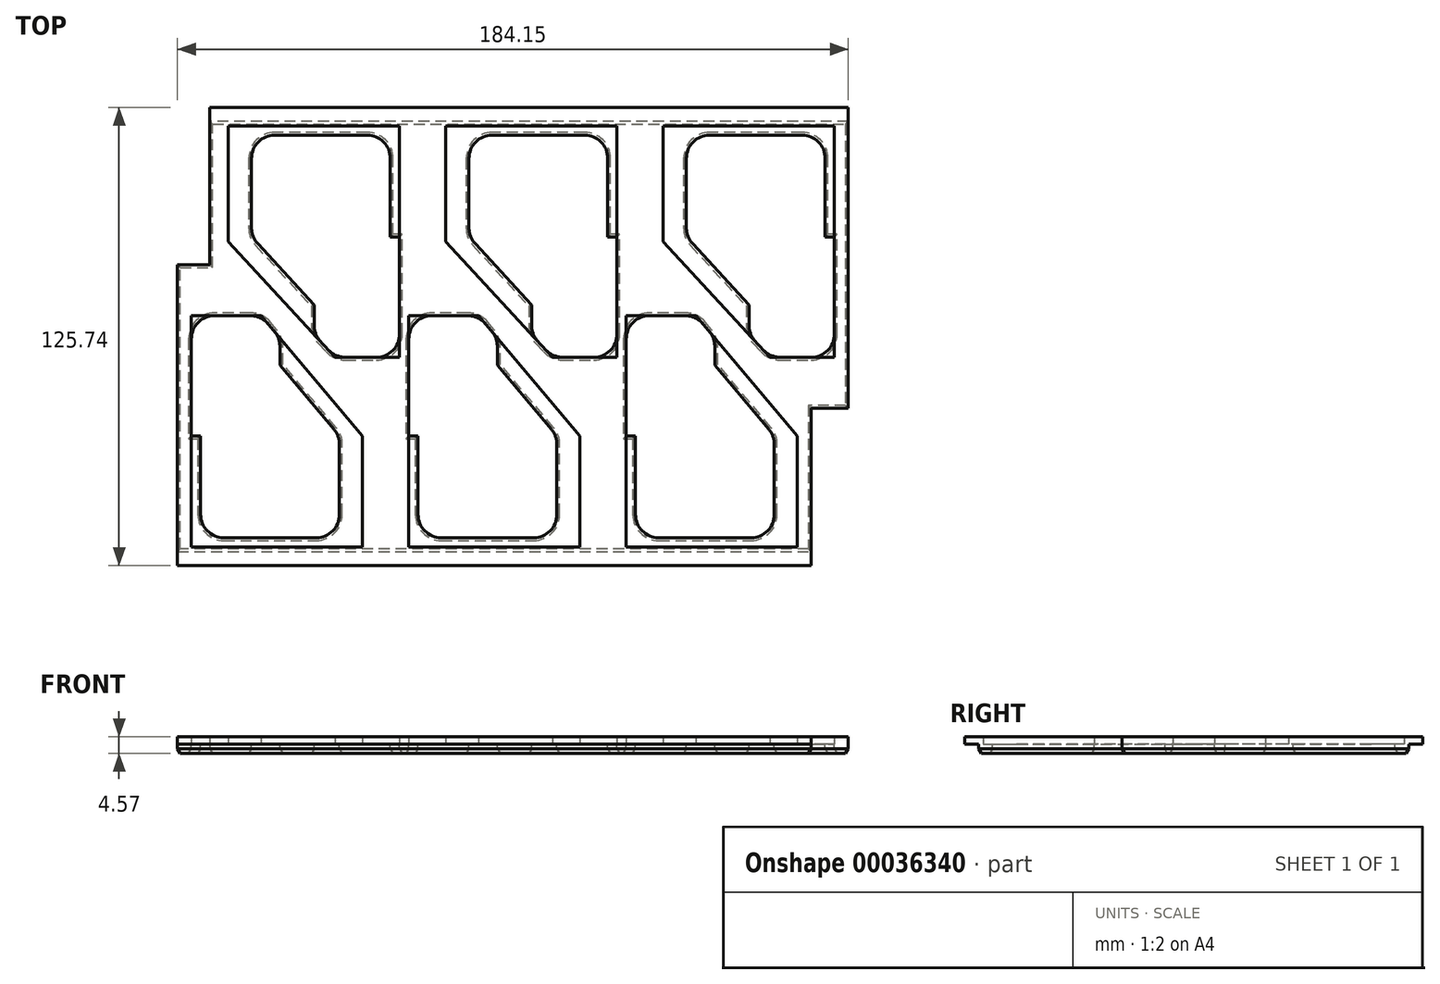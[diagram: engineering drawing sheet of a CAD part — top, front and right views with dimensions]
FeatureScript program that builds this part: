
annotation { "Feature Type Name" : "Feature", "Feature Type Description" : "" }
export const myFeature = defineFeature(function(context is Context, id is Id, definition is map)
    precondition{}
    {
        {
            var Q0;
            Q0=qCreatedBy(makeId("Top.planeOp"),FACE);
            var sketch = newSketch(context, id + "F0", { "sketchPlane" : qUnion([Q0])});
            skLineSegment(sketch, "E0.rect.bottom", {"start": v(-81.28, 62.87) * mm, "end": v(93.98, 62.87) * mm});
            skLineSegment(sketch, "E0.rect.top", {"start": v(-90.17, -62.87) * mm, "end": v(83.82, -62.87) * mm});
            skLineSegment(sketch, "E0.rect.right", {"start": v(93.98, 62.87) * mm, "end": v(93.98, -19.69) * mm});
            skPoint(sketch, "E0.rect.middle", {"position": v(0, 0) * mm});
            skLineSegment(sketch, "E1.MirrorCS", {"start": v(43.18, 57.79) * mm, "end": v(90.17, 57.79) * mm});
            skLineSegment(sketch, "E2.MirrorCS", {"start": v(72.45, -5.71) * mm, "end": v(90.17, -5.71) * mm});
            skLineSegment(sketch, "E3.MirrorCS", {"start": v(-16.51, 26.04) * mm, "end": v(12.76, -5.71) * mm});
            skLineSegment(sketch, "E4.MirrorCS", {"start": v(12.76, -5.71) * mm, "end": v(30.48, -5.71) * mm});
            skLineSegment(sketch, "E5.MirrorCS", {"start": v(-16.51, 57.79) * mm, "end": v(-16.5, 26.04) * mm});
            skLineSegment(sketch, "E6.MirrorCS", {"start": v(30.48, 57.79) * mm, "end": v(30.48, -5.71) * mm});
            skLineSegment(sketch, "E7.MirrorCS", {"start": v(-76.2, 26.04) * mm, "end": v(-46.93, -5.71) * mm});
            skLineSegment(sketch, "E8.MirrorCS", {"start": v(-76.2, 57.79) * mm, "end": v(-76.2, 26.04) * mm});
            skLineSegment(sketch, "E9.MirrorCS", {"start": v(-46.93, -5.71) * mm, "end": v(-29.21, -5.71) * mm});
            skLineSegment(sketch, "E10.MirrorCS", {"start": v(-29.21, 57.79) * mm, "end": v(-29.2, -5.71) * mm});
            skLineSegment(sketch, "E11.MirrorCS", {"start": v(-76.2, 57.79) * mm, "end": v(-29.21, 57.79) * mm});
            skLineSegment(sketch, "E12.MirrorCS", {"start": v(90.17, 57.79) * mm, "end": v(90.17, -5.71) * mm});
            skLineSegment(sketch, "E13.MirrorCS", {"start": v(43.18, 57.79) * mm, "end": v(43.18, 26.04) * mm});
            skLineSegment(sketch, "E14.MirrorCS", {"start": v(43.18, 26.04) * mm, "end": v(72.45, -5.72) * mm});
            skLineSegment(sketch, "E15.MirrorCS", {"start": v(-16.51, 57.79) * mm, "end": v(30.48, 57.79) * mm});
            skLineSegment(sketch, "E16.bottom", {"start": v(-39.37, -57.78) * mm, "end": v(-86.36, -57.79) * mm});
            skLineSegment(sketch, "E16.top", {"start": v(-67.2, 5.71) * mm, "end": v(-86.36, 5.71) * mm});
            skLineSegment(sketch, "E16.left", {"start": v(-39.37, -57.79) * mm, "end": v(-39.37, -27.3) * mm});
            skLineSegment(sketch, "E16.right", {"start": v(-86.36, -57.79) * mm, "end": v(-86.36, 5.72) * mm});
            skLineSegment(sketch, "E17", {"start": v(-67.2, 5.72) * mm, "end": v(-39.37, -27.3) * mm});
            skLineSegment(sketch, "E18.right", {"start": v(-26.67, -57.79) * mm, "end": v(-26.67, 5.72) * mm});
            skLineSegment(sketch, "E18.top", {"start": v(-7.5, 5.72) * mm, "end": v(-26.67, 5.72) * mm});
            skLineSegment(sketch, "E19", {"start": v(-7.5, 5.71) * mm, "end": v(20.32, -27.3) * mm});
            skLineSegment(sketch, "E18.left", {"start": v(20.32, -57.79) * mm, "end": v(20.32, -27.3) * mm});
            skLineSegment(sketch, "E18.bottom", {"start": v(20.32, -57.78) * mm, "end": v(-26.67, -57.78) * mm});
            skLineSegment(sketch, "E20.right", {"start": v(33.02, -57.79) * mm, "end": v(33.02, 5.72) * mm});
            skLineSegment(sketch, "E20.top", {"start": v(52.19, 5.72) * mm, "end": v(33.02, 5.72) * mm});
            skLineSegment(sketch, "E21", {"start": v(52.19, 5.72) * mm, "end": v(80.01, -27.3) * mm});
            skLineSegment(sketch, "E20.left", {"start": v(80.01, -57.79) * mm, "end": v(80.01, -27.3) * mm});
            skLineSegment(sketch, "E20.bottom", {"start": v(80.01, -57.78) * mm, "end": v(33.02, -57.79) * mm});
            skLineSegment(sketch, "E22", {"start": v(93.98, -19.69) * mm, "end": v(83.82, -19.69) * mm});
            skLineSegment(sketch, "E23", {"start": v(83.82, -19.69) * mm, "end": v(83.82, -62.87) * mm});
            skPoint(sketch, "E24.orphan", {"position": v(93.98, -62.87) * mm});
            skLineSegment(sketch, "E25", {"start": v(-81.28, 62.86) * mm, "end": v(-81.28, 19.68) * mm});
            skLineSegment(sketch, "E26", {"start": v(-81.28, 19.69) * mm, "end": v(-90.17, 19.68) * mm});
            skLineSegment(sketch, "E27", {"start": v(-90.17, 19.68) * mm, "end": v(-90.17, -62.87) * mm});
            skSolve(sketch);
        }
        {
            var Q0;
            Q0 = qSketchRegion(id + "F0", true);
            extrude(context, id + "F1", {"entities" : qUnion([Q0]), "depth" : 2.03 * mm});
        }
        {
            var Q0;
            Q0=makeQuery(id+"F1.opExtrude","CAP_FACE",FACE,{"disambiguationData":[OSD([sQuery(id+"F0.wireOp",EDGE,"E0.rect.bottom"),sQuery(id+"F0.wireOp",EDGE,"E0.rect.top"),sQuery(id+"F0.wireOp",EDGE,"E0.rect.left"),sQuery(id+"F0.wireOp",EDGE,"E0.rect.right"),sQuery(id+"F0.wireOp",EDGE,"E1.MirrorCS"),sQuery(id+"F0.wireOp",EDGE,"E2.MirrorCS"),sQuery(id+"F0.wireOp",EDGE,"E3.MirrorCS"),sQuery(id+"F0.wireOp",EDGE,"E4.MirrorCS"),sQuery(id+"F0.wireOp",EDGE,"E5.MirrorCS"),sQuery(id+"F0.wireOp",EDGE,"E6.MirrorCS"),sQuery(id+"F0.wireOp",EDGE,"E7.MirrorCS"),sQuery(id+"F0.wireOp",EDGE,"E8.MirrorCS"),sQuery(id+"F0.wireOp",EDGE,"E9.MirrorCS"),sQuery(id+"F0.wireOp",EDGE,"E10.MirrorCS"),sQuery(id+"F0.wireOp",EDGE,"E11.MirrorCS"),sQuery(id+"F0.wireOp",EDGE,"E12.MirrorCS"),sQuery(id+"F0.wireOp",EDGE,"E13.MirrorCS"),sQuery(id+"F0.wireOp",EDGE,"E14.MirrorCS"),sQuery(id+"F0.wireOp",EDGE,"E15.MirrorCS"),sQuery(id+"F0.wireOp",EDGE,"E16.bottom"),sQuery(id+"F0.wireOp",EDGE,"E16.top"),sQuery(id+"F0.wireOp",EDGE,"E16.left"),sQuery(id+"F0.wireOp",EDGE,"E16.right"),sQuery(id+"F0.wireOp",EDGE,"E17"),sQuery(id+"F0.wireOp",EDGE,"E18.right"),sQuery(id+"F0.wireOp",EDGE,"E18.top"),sQuery(id+"F0.wireOp",EDGE,"E19"),sQuery(id+"F0.wireOp",EDGE,"E18.left"),sQuery(id+"F0.wireOp",EDGE,"E18.bottom"),sQuery(id+"F0.wireOp",EDGE,"E20.right"),sQuery(id+"F0.wireOp",EDGE,"E20.top"),sQuery(id+"F0.wireOp",EDGE,"E21"),sQuery(id+"F0.wireOp",EDGE,"E20.left"),sQuery(id+"F0.wireOp",EDGE,"E20.bottom")])],"isStart":true});
            var sketch = newSketch(context, id + "F2", { "sketchPlane" : qUnion([Q0])});
            skLineSegment(sketch, "E28.bottom", {"start": v(-81.28, 62.87) * mm, "end": v(83.82, 62.87) * mm});
            skLineSegment(sketch, "E28.top", {"start": v(-81.28, -62.86) * mm, "end": v(93.98, -62.86) * mm});
            skLineSegment(sketch, "E28.right", {"start": v(93.98, 19.69) * mm, "end": v(93.98, -62.87) * mm});
            skLineSegment(sketch, "E29", {"start": v(-81.28, -62.86) * mm, "end": v(-81.28, -19.69) * mm});
            skLineSegment(sketch, "E30", {"start": v(-81.28, -19.69) * mm, "end": v(-81.28, -19.69) * mm});
            skLineSegment(sketch, "E31", {"start": v(83.82, 19.69) * mm, "end": v(83.82, 62.87) * mm});
            skLineSegment(sketch, "E32", {"start": v(83.82, 19.69) * mm, "end": v(93.98, 19.69) * mm});
            skLineSegment(sketch, "E33", {"start": v(-81.28, 62.87) * mm, "end": v(-90.17, 62.87) * mm});
            skLineSegment(sketch, "E34", {"start": v(-90.17, 62.87) * mm, "end": v(-90.17, -19.68) * mm});
            skLineSegment(sketch, "E35", {"start": v(-90.17, -19.68) * mm, "end": v(-81.28, -19.69) * mm});
            skSolve(sketch);
        }
        {
            var Q0;
            Q0 = qSketchRegion(id + "F2", true);
            extrude(context, id + "F3", {"entities" : qUnion([Q0]), "operationType" : NewBodyOperationType.ADD, "depth" : 2.54 * mm});
        }
        {
            var Q0;
            Q0=makeQuery(id+"F3.boolean.opBoolean","SPLIT",FACE,{"disambiguationData":[TD([makeQuery(id+"F1.opExtrude","SWEPT_FACE",FACE,{"disambiguationData":[OSD([sQuery(id+"F0.wireOp",EDGE,"E7.MirrorCS")])]})])],"derivedFrom":makeQuery(id+"F3.opExtrude","CAP_FACE",FACE,{"disambiguationData":[OSD([sQuery(id+"F2.wireOp",EDGE,"E28.bottom"),sQuery(id+"F2.wireOp",EDGE,"E28.top"),sQuery(id+"F2.wireOp",EDGE,"E28.left"),sQuery(id+"F2.wireOp",EDGE,"E28.right")])],"isStart":true})});
            var sketch = newSketch(context, id + "F4", { "sketchPlane" : qUnion([Q0])});
            skLineSegment(sketch, "E36", {"start": v(-69.85, 48.9) * mm, "end": v(-69.85, 29.79) * mm});
            skLineSegment(sketch, "E37", {"start": v(-68.17, 25.48) * mm, "end": v(-52.64, 8.63) * mm});
            skLineSegment(sketch, "E38", {"start": v(-44.15, -5.71) * mm, "end": v(-35.56, -5.71) * mm});
            skLineSegment(sketch, "E39", {"start": v(-29.21, 0.64) * mm, "end": v(-29.21, 27.3) * mm});
            skLineSegment(sketch, "E40", {"start": v(-29.2, 27.3) * mm, "end": v(-31.75, 27.3) * mm});
            skLineSegment(sketch, "E41", {"start": v(-31.75, 27.3) * mm, "end": v(-31.75, 48.9) * mm});
            skLineSegment(sketch, "E42", {"start": v(-38.1, 55.25) * mm, "end": v(-63.5, 55.25) * mm});
            skLineSegment(sketch, "E43", {"start": v(-52.64, 8.63) * mm, "end": v(-52.64, 2.95) * mm});
            skLineSegment(sketch, "E44", {"start": v(-50.95, -1.35) * mm, "end": v(-48.82, -3.67) * mm});
            skLineSegment(sketch, "E45", {"start": v(-10.16, 48.9) * mm, "end": v(-10.16, 29.79) * mm});
            skLineSegment(sketch, "E46", {"start": v(-8.48, 25.48) * mm, "end": v(7.05, 8.63) * mm});
            skLineSegment(sketch, "E47", {"start": v(15.54, -5.71) * mm, "end": v(24.13, -5.71) * mm});
            skLineSegment(sketch, "E48", {"start": v(8.74, -1.35) * mm, "end": v(10.87, -3.67) * mm});
            skLineSegment(sketch, "E49", {"start": v(21.6, 55.25) * mm, "end": v(-3.8, 55.25) * mm});
            skLineSegment(sketch, "E50", {"start": v(7.05, 8.63) * mm, "end": v(7.05, 2.95) * mm});
            skLineSegment(sketch, "E51", {"start": v(30.48, 0.64) * mm, "end": v(30.48, 27.3) * mm});
            skLineSegment(sketch, "E52", {"start": v(27.94, 27.3) * mm, "end": v(27.94, 48.9) * mm});
            skLineSegment(sketch, "E53", {"start": v(30.48, 27.3) * mm, "end": v(27.94, 27.3) * mm});
            skLineSegment(sketch, "E54", {"start": v(49.53, 48.9) * mm, "end": v(49.53, 29.79) * mm});
            skLineSegment(sketch, "E55", {"start": v(75.23, -5.72) * mm, "end": v(83.82, -5.71) * mm});
            skLineSegment(sketch, "E56", {"start": v(81.28, 55.25) * mm, "end": v(55.88, 55.25) * mm});
            skLineSegment(sketch, "E57", {"start": v(87.63, 27.3) * mm, "end": v(87.63, 48.9) * mm});
            skLineSegment(sketch, "E58", {"start": v(66.74, 8.63) * mm, "end": v(66.74, 2.95) * mm});
            skLineSegment(sketch, "E59", {"start": v(68.43, -1.35) * mm, "end": v(70.56, -3.67) * mm});
            skLineSegment(sketch, "E60", {"start": v(90.17, 0.64) * mm, "end": v(90.17, 27.3) * mm});
            skLineSegment(sketch, "E61", {"start": v(51.21, 25.48) * mm, "end": v(66.74, 8.63) * mm});
            skLineSegment(sketch, "E62", {"start": v(90.17, 27.3) * mm, "end": v(87.63, 27.3) * mm});
            skLineSegment(sketch, "E63", {"start": v(-77.47, -55.25) * mm, "end": v(-52.07, -55.24) * mm});
            skLineSegment(sketch, "E64", {"start": v(-45.72, -48.9) * mm, "end": v(-45.72, -29.62) * mm});
            skLineSegment(sketch, "E65", {"start": v(-47.21, -25.53) * mm, "end": v(-62.09, -7.88) * mm});
            skLineSegment(sketch, "E66", {"start": v(-62.09, -7.88) * mm, "end": v(-62.09, -2.66) * mm});
            skLineSegment(sketch, "E67", {"start": v(-63.58, 1.43) * mm, "end": v(-65.3, 3.46) * mm});
            skLineSegment(sketch, "E68", {"start": v(-70.15, 5.72) * mm, "end": v(-80, 5.72) * mm});
            skLineSegment(sketch, "E69", {"start": v(-86.36, -0.63) * mm, "end": v(-86.36, -27.3) * mm});
            skLineSegment(sketch, "E70", {"start": v(-86.36, -27.3) * mm, "end": v(-83.82, -27.3) * mm});
            skLineSegment(sketch, "E71", {"start": v(-83.82, -27.3) * mm, "end": v(-83.82, -48.9) * mm});
            skLineSegment(sketch, "E72", {"start": v(12.48, -25.53) * mm, "end": v(-2.4, -7.88) * mm});
            skLineSegment(sketch, "E73", {"start": v(-26.67, -0.64) * mm, "end": v(-26.67, -27.3) * mm});
            skLineSegment(sketch, "E74", {"start": v(-2.4, -7.88) * mm, "end": v(-2.4, -2.66) * mm});
            skLineSegment(sketch, "E75", {"start": v(-10.46, 5.71) * mm, "end": v(-20.32, 5.71) * mm});
            skLineSegment(sketch, "E76", {"start": v(13.97, -48.9) * mm, "end": v(13.97, -29.62) * mm});
            skLineSegment(sketch, "E77", {"start": v(-17.78, -55.24) * mm, "end": v(7.62, -55.24) * mm});
            skLineSegment(sketch, "E78", {"start": v(-24.13, -27.3) * mm, "end": v(-24.13, -48.9) * mm});
            skLineSegment(sketch, "E79", {"start": v(-3.9, 1.43) * mm, "end": v(-5.6, 3.46) * mm});
            skLineSegment(sketch, "E80", {"start": v(-26.67, -27.3) * mm, "end": v(-24.13, -27.3) * mm});
            skLineSegment(sketch, "E81", {"start": v(55.8, 1.43) * mm, "end": v(54.09, 3.46) * mm});
            skLineSegment(sketch, "E82", {"start": v(57.3, -7.88) * mm, "end": v(57.3, -2.66) * mm});
            skLineSegment(sketch, "E83", {"start": v(72.17, -25.53) * mm, "end": v(57.3, -7.88) * mm});
            skLineSegment(sketch, "E84", {"start": v(49.23, 5.72) * mm, "end": v(39.37, 5.72) * mm});
            skLineSegment(sketch, "E85", {"start": v(33.02, -0.63) * mm, "end": v(33.02, -27.3) * mm});
            skLineSegment(sketch, "E86", {"start": v(73.66, -48.9) * mm, "end": v(73.66, -29.62) * mm});
            skLineSegment(sketch, "E87", {"start": v(41.91, -55.25) * mm, "end": v(67.31, -55.24) * mm});
            skLineSegment(sketch, "E88", {"start": v(35.56, -27.3) * mm, "end": v(35.56, -48.9) * mm});
            skLineSegment(sketch, "E89", {"start": v(33.02, -27.3) * mm, "end": v(35.56, -27.3) * mm});
            skPoint(sketch, "E90.visualSharp", {"position": v(-69.85, 55.25) * mm});
            skArc(sketch, "E90.filletArc", {"start": v(-63.5, 55.25) * mm, "mid": v(-68, 53.39) * mm, "end": v(-69.85, 48.9) * mm});
            skPoint(sketch, "E91.visualSharp", {"position": v(-31.75, 55.25) * mm});
            skArc(sketch, "E91.filletArc", {"start": v(-31.75, 48.9) * mm, "mid": v(-33.6, 53.39) * mm, "end": v(-38.1, 55.25) * mm});
            skPoint(sketch, "E92.visualSharp", {"position": v(-69.85, 27.3) * mm});
            skArc(sketch, "E92.filletArc", {"start": v(-69.85, 29.79) * mm, "mid": v(-69.41, 27.47) * mm, "end": v(-68.17, 25.48) * mm});
            skPoint(sketch, "E93.visualSharp", {"position": v(-52.64, 0.47) * mm});
            skArc(sketch, "E93.filletArc", {"start": v(-52.64, 2.95) * mm, "mid": v(-52.2, 0.64) * mm, "end": v(-50.95, -1.35) * mm});
            skPoint(sketch, "E94.visualSharp", {"position": v(-46.93, -5.71) * mm});
            skArc(sketch, "E94.filletArc", {"start": v(-48.82, -3.67) * mm, "mid": v(-46.7, -5.18) * mm, "end": v(-44.15, -5.71) * mm});
            skPoint(sketch, "E95.visualSharp", {"position": v(-29.2, -5.71) * mm});
            skArc(sketch, "E95.filletArc", {"start": v(-35.56, -5.71) * mm, "mid": v(-31.07, -3.86) * mm, "end": v(-29.2, 0.64) * mm});
            skPoint(sketch, "E96.visualSharp", {"position": v(-10.16, 55.25) * mm});
            skArc(sketch, "E96.filletArc", {"start": v(-3.8, 55.25) * mm, "mid": v(-8.3, 53.39) * mm, "end": v(-10.16, 48.9) * mm});
            skPoint(sketch, "E97.visualSharp", {"position": v(27.94, 55.25) * mm});
            skArc(sketch, "E97.filletArc", {"start": v(27.94, 48.9) * mm, "mid": v(26.08, 53.39) * mm, "end": v(21.6, 55.25) * mm});
            skPoint(sketch, "E98.visualSharp", {"position": v(-10.16, 27.3) * mm});
            skArc(sketch, "E98.filletArc", {"start": v(-10.16, 29.79) * mm, "mid": v(-9.72, 27.47) * mm, "end": v(-8.48, 25.48) * mm});
            skPoint(sketch, "E99.visualSharp", {"position": v(7.05, 0.47) * mm});
            skArc(sketch, "E99.filletArc", {"start": v(7.05, 2.95) * mm, "mid": v(7.49, 0.64) * mm, "end": v(8.74, -1.35) * mm});
            skPoint(sketch, "E100.visualSharp", {"position": v(12.76, -5.71) * mm});
            skArc(sketch, "E100.filletArc", {"start": v(10.87, -3.67) * mm, "mid": v(12.99, -5.18) * mm, "end": v(15.54, -5.71) * mm});
            skPoint(sketch, "E101.visualSharp", {"position": v(30.48, -5.71) * mm});
            skArc(sketch, "E101.filletArc", {"start": v(24.13, -5.71) * mm, "mid": v(28.62, -3.86) * mm, "end": v(30.48, 0.64) * mm});
            skPoint(sketch, "E102.visualSharp", {"position": v(49.53, 55.25) * mm});
            skArc(sketch, "E102.filletArc", {"start": v(55.88, 55.25) * mm, "mid": v(51.39, 53.39) * mm, "end": v(49.53, 48.9) * mm});
            skPoint(sketch, "E103.visualSharp", {"position": v(87.63, 55.25) * mm});
            skArc(sketch, "E103.filletArc", {"start": v(87.63, 48.9) * mm, "mid": v(85.77, 53.39) * mm, "end": v(81.28, 55.25) * mm});
            skPoint(sketch, "E104.visualSharp", {"position": v(49.53, 27.3) * mm});
            skArc(sketch, "E104.filletArc", {"start": v(49.53, 29.79) * mm, "mid": v(49.97, 27.47) * mm, "end": v(51.21, 25.48) * mm});
            skPoint(sketch, "E105.visualSharp", {"position": v(66.74, 0.47) * mm});
            skArc(sketch, "E105.filletArc", {"start": v(66.74, 2.95) * mm, "mid": v(67.18, 0.64) * mm, "end": v(68.43, -1.35) * mm});
            skPoint(sketch, "E106.visualSharp", {"position": v(72.45, -5.72) * mm});
            skArc(sketch, "E106.filletArc", {"start": v(70.56, -3.67) * mm, "mid": v(72.68, -5.18) * mm, "end": v(75.23, -5.72) * mm});
            skPoint(sketch, "E107.visualSharp", {"position": v(90.17, -5.71) * mm});
            skArc(sketch, "E107.filletArc", {"start": v(83.82, -5.71) * mm, "mid": v(88.31, -3.86) * mm, "end": v(90.17, 0.64) * mm});
            skPoint(sketch, "E108.visualSharp", {"position": v(33.02, 5.72) * mm});
            skArc(sketch, "E108.filletArc", {"start": v(39.37, 5.72) * mm, "mid": v(34.88, 3.86) * mm, "end": v(33.02, -0.63) * mm});
            skPoint(sketch, "E109.visualSharp", {"position": v(52.19, 5.72) * mm});
            skArc(sketch, "E109.filletArc", {"start": v(54.09, 3.46) * mm, "mid": v(51.91, 5.12) * mm, "end": v(49.23, 5.72) * mm});
            skPoint(sketch, "E110.visualSharp", {"position": v(57.3, -0.35) * mm});
            skArc(sketch, "E110.filletArc", {"start": v(57.3, -2.66) * mm, "mid": v(56.9, -0.49) * mm, "end": v(55.8, 1.43) * mm});
            skPoint(sketch, "E111.visualSharp", {"position": v(73.66, -27.3) * mm});
            skArc(sketch, "E111.filletArc", {"start": v(73.66, -29.62) * mm, "mid": v(73.27, -27.45) * mm, "end": v(72.17, -25.53) * mm});
            skPoint(sketch, "E112.visualSharp", {"position": v(73.66, -55.24) * mm});
            skArc(sketch, "E112.filletArc", {"start": v(67.31, -55.25) * mm, "mid": v(71.8, -53.39) * mm, "end": v(73.66, -48.9) * mm});
            skPoint(sketch, "E113.visualSharp", {"position": v(35.56, -55.25) * mm});
            skArc(sketch, "E113.filletArc", {"start": v(35.56, -48.9) * mm, "mid": v(37.42, -53.39) * mm, "end": v(41.91, -55.25) * mm});
            skPoint(sketch, "E114.visualSharp", {"position": v(13.97, -55.24) * mm});
            skArc(sketch, "E114.filletArc", {"start": v(7.62, -55.24) * mm, "mid": v(12.11, -53.39) * mm, "end": v(13.97, -48.9) * mm});
            skPoint(sketch, "E115.visualSharp", {"position": v(-24.13, -55.24) * mm});
            skArc(sketch, "E115.filletArc", {"start": v(-24.13, -48.9) * mm, "mid": v(-22.27, -53.39) * mm, "end": v(-17.78, -55.25) * mm});
            skPoint(sketch, "E116.visualSharp", {"position": v(13.97, -27.3) * mm});
            skArc(sketch, "E116.filletArc", {"start": v(13.97, -29.62) * mm, "mid": v(13.58, -27.45) * mm, "end": v(12.48, -25.53) * mm});
            skPoint(sketch, "E117.visualSharp", {"position": v(-2.4, -0.35) * mm});
            skArc(sketch, "E117.filletArc", {"start": v(-2.4, -2.66) * mm, "mid": v(-2.78, -0.49) * mm, "end": v(-3.9, 1.43) * mm});
            skPoint(sketch, "E118.visualSharp", {"position": v(-7.5, 5.71) * mm});
            skArc(sketch, "E118.filletArc", {"start": v(-5.6, 3.46) * mm, "mid": v(-7.78, 5.12) * mm, "end": v(-10.46, 5.71) * mm});
            skPoint(sketch, "E119.visualSharp", {"position": v(-26.67, 5.72) * mm});
            skArc(sketch, "E119.filletArc", {"start": v(-20.32, 5.71) * mm, "mid": v(-24.81, 3.86) * mm, "end": v(-26.67, -0.64) * mm});
            skPoint(sketch, "E120.visualSharp", {"position": v(-45.72, -55.24) * mm});
            skArc(sketch, "E120.filletArc", {"start": v(-52.07, -55.25) * mm, "mid": v(-47.58, -53.39) * mm, "end": v(-45.72, -48.9) * mm});
            skPoint(sketch, "E121.visualSharp", {"position": v(-45.72, -27.3) * mm});
            skArc(sketch, "E121.filletArc", {"start": v(-45.72, -29.62) * mm, "mid": v(-46.1, -27.45) * mm, "end": v(-47.21, -25.53) * mm});
            skPoint(sketch, "E122.visualSharp", {"position": v(-62.09, -0.35) * mm});
            skArc(sketch, "E122.filletArc", {"start": v(-62.09, -2.66) * mm, "mid": v(-62.47, -0.49) * mm, "end": v(-63.58, 1.43) * mm});
            skPoint(sketch, "E123.visualSharp", {"position": v(-67.2, 5.72) * mm});
            skArc(sketch, "E123.filletArc", {"start": v(-65.3, 3.46) * mm, "mid": v(-67.47, 5.12) * mm, "end": v(-70.15, 5.72) * mm});
            skPoint(sketch, "E124.visualSharp", {"position": v(-86.36, 5.72) * mm});
            skArc(sketch, "E124.filletArc", {"start": v(-80, 5.72) * mm, "mid": v(-84.5, 3.86) * mm, "end": v(-86.36, -0.63) * mm});
            skPoint(sketch, "E125.visualSharp", {"position": v(-83.82, -55.25) * mm});
            skArc(sketch, "E125.filletArc", {"start": v(-83.82, -48.9) * mm, "mid": v(-81.96, -53.39) * mm, "end": v(-77.47, -55.24) * mm});
            skSolve(sketch);
        }
        {
            var Q0;
            Q0 = qSketchRegion(id + "F4", true);
            extrude(context, id + "F5", {"entities" : qUnion([Q0]), "operationType" : NewBodyOperationType.REMOVE, "oppositeDirection" : true, "depth" : 25.4 * mm});
        }
        {
            var Q0;
            Q0=makeQuery(id+"F3.opExtrude","CAP_FACE",FACE,{"disambiguationData":[OSD([sQuery(id+"F2.wireOp",EDGE,"E28.bottom"),sQuery(id+"F2.wireOp",EDGE,"E28.top"),sQuery(id+"F2.wireOp",EDGE,"E28.left"),sQuery(id+"F2.wireOp",EDGE,"E28.right"),sQuery(id+"F2.wireOp",EDGE,"E29"),sQuery(id+"F2.wireOp",EDGE,"E30"),sQuery(id+"F2.wireOp",EDGE,"E31"),sQuery(id+"F2.wireOp",EDGE,"E32")])],"isStart":false});
            var sketch = newSketch(context, id + "F8", { "sketchPlane" : qUnion([Q0])});
            skLineSegment(sketch, "E126", {"start": v(-81.28, -59.06) * mm, "end": v(93.98, -59.05) * mm});
            skLineSegment(sketch, "E127", {"start": v(93.98, -59.05) * mm, "end": v(93.98, -62.87) * mm});
            skLineSegment(sketch, "E128", {"start": v(93.98, -62.87) * mm, "end": v(-81.28, -62.87) * mm});
            skLineSegment(sketch, "E129", {"start": v(-81.28, -62.86) * mm, "end": v(-81.28, -59.06) * mm});
            skLineSegment(sketch, "E130.bottom", {"start": v(-90.17, 59.06) * mm, "end": v(83.82, 59.06) * mm});
            skLineSegment(sketch, "E130.top", {"start": v(-90.17, 62.87) * mm, "end": v(83.82, 62.87) * mm});
            skLineSegment(sketch, "E130.left", {"start": v(-90.17, 59.06) * mm, "end": v(-90.17, 62.87) * mm});
            skLineSegment(sketch, "E130.right", {"start": v(83.82, 59.06) * mm, "end": v(83.82, 62.87) * mm});
            skSolve(sketch);
        }
        {
            var Q0;
            Q0 = qSketchRegion(id + "F8", true);
            extrude(context, id + "F9", {"entities" : qUnion([Q0]), "operationType" : NewBodyOperationType.REMOVE, "oppositeDirection" : true, "depth" : 2.54 * mm});
        }
        {
            var Q0;
            Q0=makeQuery(id+"F3.opExtrude","CAP_FACE",FACE,{"disambiguationData":[OSD([sQuery(id+"F2.wireOp",EDGE,"E28.bottom"),sQuery(id+"F2.wireOp",EDGE,"E28.top"),sQuery(id+"F2.wireOp",EDGE,"E28.right"),sQuery(id+"F2.wireOp",EDGE,"E29"),sQuery(id+"F2.wireOp",EDGE,"E31"),sQuery(id+"F2.wireOp",EDGE,"E32"),sQuery(id+"F2.wireOp",EDGE,"E33"),sQuery(id+"F2.wireOp",EDGE,"E34"),sQuery(id+"F2.wireOp",EDGE,"E35")])],"isStart":false});
            chamfer(context, id + "F10", {"entities" : qUnion([Q0]), "chamferType" : ChamferType.OFFSET_ANGLE, "width" : 0.76 * mm, "oppositeDirection" : false, "angle" : 60 * degree, "tangentPropagation" : true});
        }
    });
